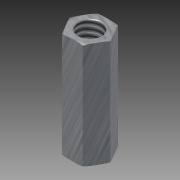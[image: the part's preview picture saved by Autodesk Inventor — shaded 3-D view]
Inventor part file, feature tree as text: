
AUTODESK INVENTOR PART (.ipt)
format: ipt  version: 2011 (Build 150239000, 239)  size: 120,832 bytes
history: native  units: in
note: dims shown in document units (in); Inventor stores cm internally (conversion verified against a paired STEP export)
features: other x1, imported_body x1, thread x1
ambient origin geometry x8: Origin, YZ Plane, XZ Plane, XY Plane, X Axis, Y Axis, Z Axis, Center Point
feature tree (3):
  parser-record x1  (decoder bookkeeping rows leaked as tree rows — omitted from the tree; the rows remain in map.json)
  imported_body  "Base1"
  thread  "Thread1"  [1 undecoded]
note: 1 required parameter value undecoded (feature->parameter linkage not recoverable at this tier; creation-order binding heuristic only, values carry confidence <= 0.55)
